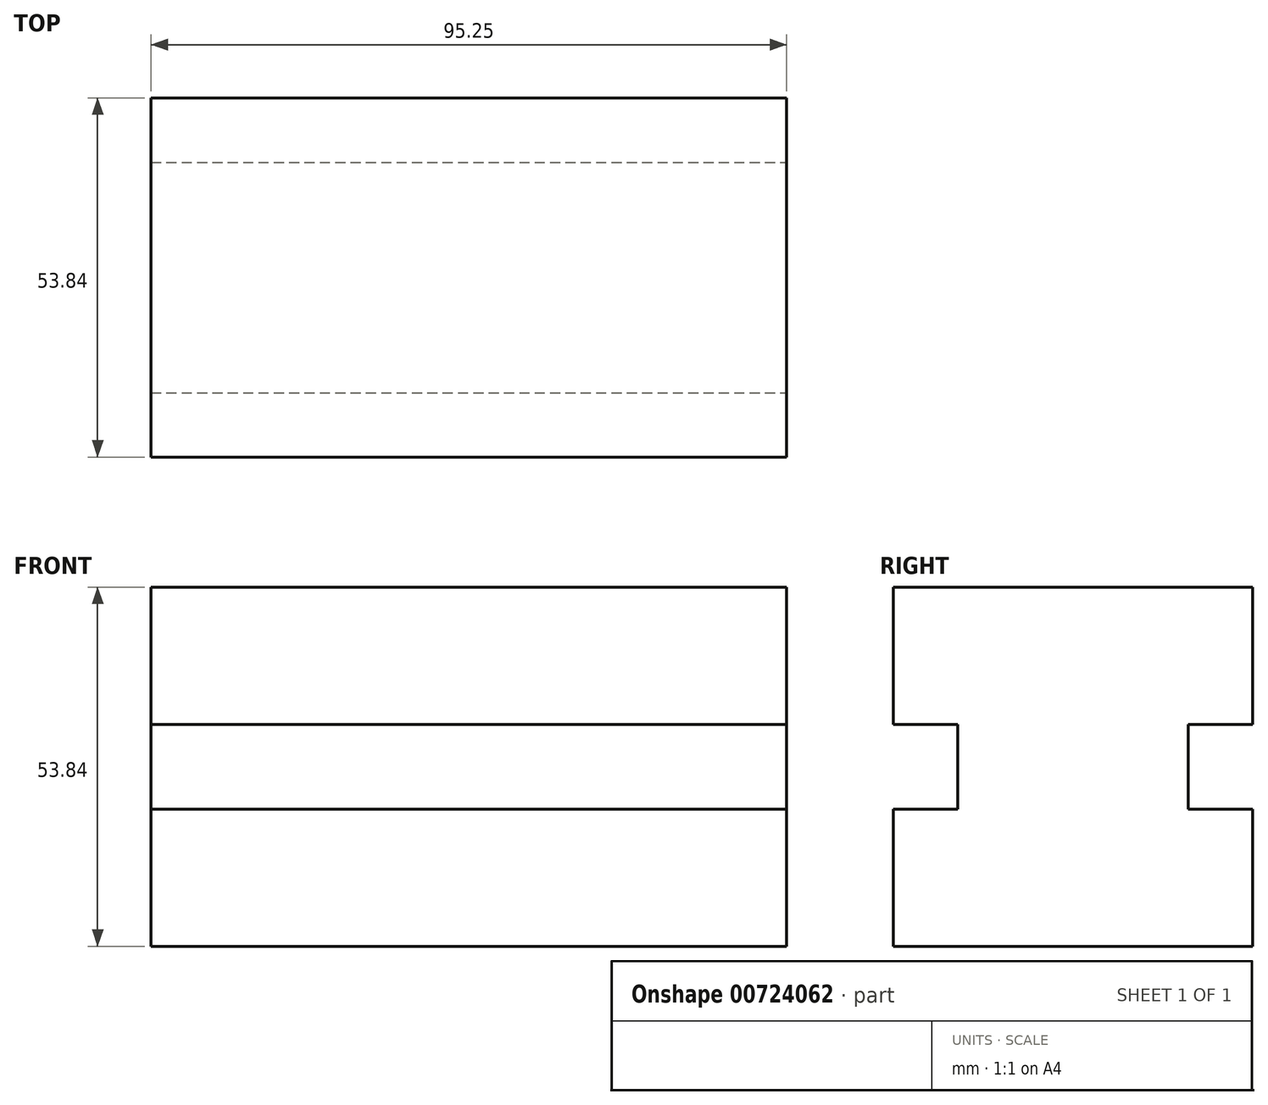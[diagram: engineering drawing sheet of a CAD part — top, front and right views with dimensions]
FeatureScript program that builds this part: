
annotation { "Feature Type Name" : "Feature", "Feature Type Description" : "" }
export const myFeature = defineFeature(function(context is Context, id is Id, definition is map)
    precondition{}
    {
        {
            var Q0;
            Q0=qCreatedBy(makeId("Right.planeOp"),FACE);
            var sketch = newSketch(context, id + "F0", { "sketchPlane" : qUnion([Q0])});
            skLineSegment(sketch, "E0.bottom", {"start": v(26.92, 26.92) * mm, "end": v(-26.92, 26.92) * mm});
            skLineSegment(sketch, "E0.top", {"start": v(26.92, -26.92) * mm, "end": v(-26.92, -26.92) * mm});
            skLineSegment(sketch, "E0.left", {"start": v(26.92, 26.92) * mm, "end": v(26.92, 6.35) * mm});
            skLineSegment(sketch, "E0.right", {"start": v(-26.92, 26.92) * mm, "end": v(-26.92, 6.35) * mm});
            skPoint(sketch, "E0.middle", {"position": v(0, 0) * mm});
            skLineSegment(sketch, "E1.bottom", {"start": v(-26.92, 6.35) * mm, "end": v(-17.27, 6.35) * mm});
            skLineSegment(sketch, "E1.top", {"start": v(-26.92, -6.35) * mm, "end": v(-17.27, -6.35) * mm});
            skLineSegment(sketch, "E1.right", {"start": v(-17.27, 6.35) * mm, "end": v(-17.27, -6.35) * mm});
            skLineSegment(sketch, "E2.bottom", {"start": v(26.92, 6.35) * mm, "end": v(17.27, 6.35) * mm});
            skLineSegment(sketch, "E2.top", {"start": v(26.92, -6.35) * mm, "end": v(17.27, -6.35) * mm});
            skLineSegment(sketch, "E2.right", {"start": v(17.27, 6.35) * mm, "end": v(17.27, -6.35) * mm});
            skLineSegment(sketch, "E3.trimOffspring", {"start": v(-26.92, -6.35) * mm, "end": v(-26.92, -26.92) * mm});
            skLineSegment(sketch, "E4.trimOffspring", {"start": v(26.92, -6.35) * mm, "end": v(26.92, -26.92) * mm});
            skLineSegment(sketch, "E5", {"start": v(0, 50.36) * mm, "end": v(0, -58.96) * mm, "construction": true});
            skSolve(sketch);
        }
        {
            var Q0;
            Q0=makeQuery(id+"F0.imprint","IMPRINT",FACE,{"disambiguationData":[TD([[makeQuery(id+"F0.imprint","IMPRINT",EDGE,{"derivedFrom":sQuery(id+"F0.wireOp",EDGE,"E0.bottom")}),1.0]])]});
            extrude(context, id + "F1", {"entities" : qUnion([Q0]), "oppositeDirection" : true, "depth" : 95.25 * mm, "offsetDistance" : 25.4 * mm});
        }
    });
